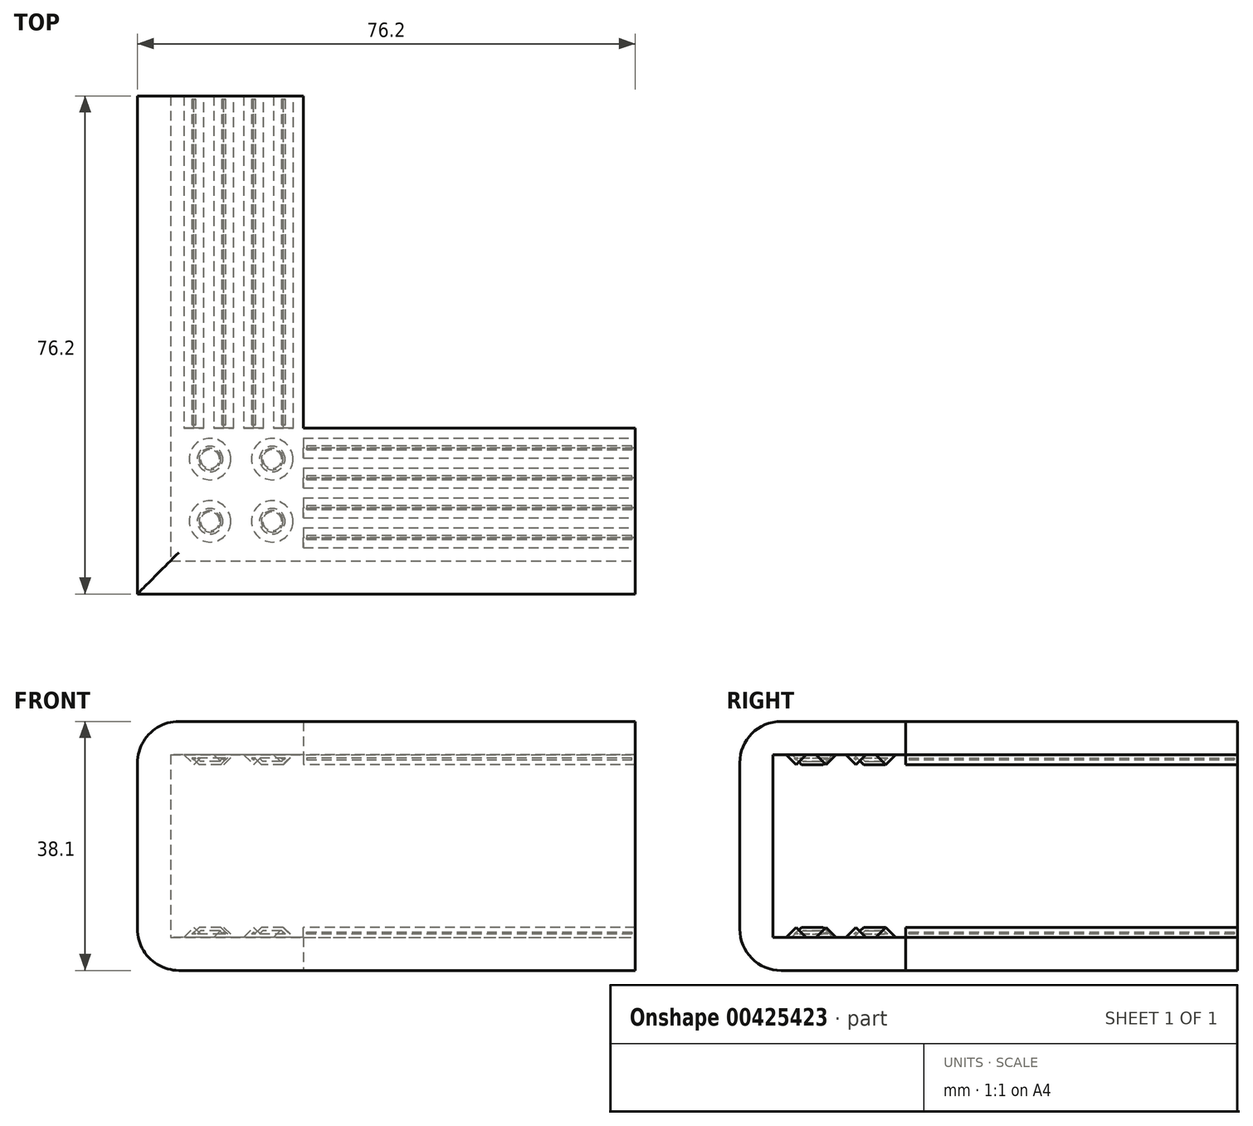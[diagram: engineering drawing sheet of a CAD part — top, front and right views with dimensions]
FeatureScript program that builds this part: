
annotation { "Feature Type Name" : "Feature", "Feature Type Description" : "" }
export const myFeature = defineFeature(function(context is Context, id is Id, definition is map)
    precondition{}
    {
        {
            var Q0;
            Q0=qCreatedBy(makeId("Top.planeOp"),FACE);
            var sketch = newSketch(context, id + "F0", { "sketchPlane" : qUnion([Q0])});
            skLineSegment(sketch, "E0", {"start": v(-49.11, 50.8) * mm, "end": v(-49.11, -25.4) * mm});
            skLineSegment(sketch, "E1", {"start": v(-49.11, -25.4) * mm, "end": v(27.09, -25.4) * mm});
            skLineSegment(sketch, "E2", {"start": v(27.09, -25.4) * mm, "end": v(27.09, 0) * mm});
            skLineSegment(sketch, "E3", {"start": v(27.09, 0) * mm, "end": v(-23.71, 0) * mm});
            skLineSegment(sketch, "E4", {"start": v(-23.71, 0) * mm, "end": v(-23.71, 50.8) * mm});
            skLineSegment(sketch, "E5", {"start": v(-23.71, 50.8) * mm, "end": v(-49.11, 50.8) * mm});
            skSolve(sketch);
        }
        {
            var Q0;
            Q0=makeQuery(id+"F0.imprint","IMPRINT",FACE,{"disambiguationData":[TD([[makeQuery(id+"F0.imprint","IMPRINT",EDGE,{"derivedFrom":sQuery(id+"F0.wireOp",EDGE,"E0")}),1.0]])]});
            extrude(context, id + "F1", {"entities" : qUnion([Q0]), "depth" : 38.1 * mm});
        }
        {
            var Q0;
            Q0=makeQuery(id+"F1.opExtrude","SWEPT_FACE",FACE,{"disambiguationData":[OSD([sQuery(id+"F0.wireOp",EDGE,"E3")])]});
            var Q1;
            Q1=makeQuery(id+"F1.opExtrude","SWEPT_FACE",FACE,{"disambiguationData":[OSD([sQuery(id+"F0.wireOp",EDGE,"E4")])]});
            var Q2;
            Q2=makeQuery(id+"F1.opExtrude","SWEPT_FACE",FACE,{"disambiguationData":[OSD([sQuery(id+"F0.wireOp",EDGE,"E2")])]});
            var Q3;
            Q3=makeQuery(id+"F1.opExtrude","SWEPT_FACE",FACE,{"disambiguationData":[OSD([sQuery(id+"F0.wireOp",EDGE,"E5")])]});
            shell(context, id + "F2", {"entities" : qUnion([Q0, Q1, Q2, Q3]), "thickness" : 5.08 * mm});
        }
        {
            var Q0;
            Q0=makeQuery(id+"F1.opExtrude","CAP_EDGE",EDGE,{"disambiguationData":[OSD([sQuery(id+"F0.wireOp",EDGE,"E1")])],"isStart":false});
            var Q1;
            Q1=makeQuery(id+"F1.opExtrude","CAP_EDGE",EDGE,{"disambiguationData":[OSD([sQuery(id+"F0.wireOp",EDGE,"E0")])],"isStart":false});
            fillet(context, id + "F3", {"entities" : qUnion([Q0, Q1]), "radius" : 6.35 * mm, "tangentPropagation" : true, "allowEdgeOverflow" : false});
        }
        {
            var Q0;
            Q0=makeQuery(id+"F1.opExtrude","CAP_EDGE",EDGE,{"disambiguationData":[OSD([sQuery(id+"F0.wireOp",EDGE,"E0")])],"isStart":true});
            var Q1;
            Q1=makeQuery(id+"F1.opExtrude","CAP_EDGE",EDGE,{"disambiguationData":[OSD([sQuery(id+"F0.wireOp",EDGE,"E1")])],"isStart":true});
            fillet(context, id + "F4", {"entities" : qUnion([Q0, Q1]), "radius" : 6.35 * mm, "tangentPropagation" : true, "allowEdgeOverflow" : false});
        }
        {
            var Q0;
            {var subQ0=sQuery(id+"F0.wireOp",EDGE,"E5");var subQ1=sQuery(id+"F0.wireOp",EDGE,"E4");var subQ2=sQuery(id+"F0.wireOp",EDGE,"E3");var subQ3=sQuery(id+"F0.wireOp",EDGE,"E2");var subQ4=sQuery(id+"F0.wireOp",EDGE,"E1");var subQ5=sQuery(id+"F0.wireOp",EDGE,"E0");Q0=makeQuery(id+"F2.opShell","OFFSET_FACE",FACE,{"disambiguationData":[OSD([subQ5,subQ4,subQ3,subQ2,subQ1,subQ0]),TDD([makeQuery(id+"F1.opExtrude","CAP_FACE",FACE,{"disambiguationData":[OSD([subQ5,subQ4,subQ3,subQ2,subQ1,subQ0])],"isStart":true})])]});}
            var sketch = newSketch(context, id + "F5", { "sketchPlane" : qUnion([Q0])});
            skLineSegment(sketch, "E6", {"start": v(-28.29, 50.8) * mm, "end": v(-25.24, 50.8) * mm});
            skLineSegment(sketch, "E7", {"start": v(-28.29, 50.8) * mm, "end": v(-28.29, 0) * mm});
            skLineSegment(sketch, "E8", {"start": v(-28.29, 0) * mm, "end": v(-25.24, 0) * mm});
            skLineSegment(sketch, "E9", {"start": v(-25.24, 0) * mm, "end": v(-25.24, 50.8) * mm});
            skLineSegment(sketch, "E10.bottom", {"start": v(-23.71, -1.52) * mm, "end": v(27.09, -1.52) * mm});
            skLineSegment(sketch, "E10.top", {"start": v(-23.71, -4.57) * mm, "end": v(27.09, -4.57) * mm});
            skLineSegment(sketch, "E10.left", {"start": v(-23.71, -1.52) * mm, "end": v(-23.71, -4.57) * mm});
            skLineSegment(sketch, "E10.right", {"start": v(27.09, -1.52) * mm, "end": v(27.09, -4.57) * mm});
            skLineSegment(sketch, "E11.0.1.0", {"start": v(-23.71, -6.1) * mm, "end": v(27.09, -6.1) * mm});
            skLineSegment(sketch, "E11.0.1.1", {"start": v(27.09, -6.1) * mm, "end": v(27.09, -9.14) * mm});
            skLineSegment(sketch, "E11.0.1.2", {"start": v(-23.71, -6.1) * mm, "end": v(-23.71, -9.14) * mm});
            skLineSegment(sketch, "E11.0.1.3", {"start": v(-23.71, -9.14) * mm, "end": v(27.09, -9.14) * mm});
            skLineSegment(sketch, "E11.0.2.0", {"start": v(-23.71, -10.67) * mm, "end": v(27.09, -10.67) * mm});
            skLineSegment(sketch, "E11.0.2.1", {"start": v(27.09, -10.67) * mm, "end": v(27.09, -13.72) * mm});
            skLineSegment(sketch, "E11.0.2.2", {"start": v(-23.71, -10.67) * mm, "end": v(-23.71, -13.72) * mm});
            skLineSegment(sketch, "E11.0.2.3", {"start": v(-23.71, -13.72) * mm, "end": v(27.09, -13.72) * mm});
            skLineSegment(sketch, "E11.0.3.0", {"start": v(-23.71, -15.24) * mm, "end": v(27.09, -15.24) * mm});
            skLineSegment(sketch, "E11.0.3.1", {"start": v(27.09, -15.24) * mm, "end": v(27.09, -18.29) * mm});
            skLineSegment(sketch, "E11.0.3.2", {"start": v(-23.71, -15.24) * mm, "end": v(-23.71, -18.29) * mm});
            skLineSegment(sketch, "E11.0.3.3", {"start": v(-23.71, -18.29) * mm, "end": v(27.09, -18.29) * mm});
            skLineSegment(sketch, "E11.direction1", {"start": v(-23.72, -4.57) * mm, "end": v(-23.71, -4.57) * mm, "construction": true});
            skLineSegment(sketch, "E11.direction2", {"start": v(-23.71, -4.57) * mm, "end": v(-23.71, -9.14) * mm, "construction": true});
            skLineSegment(sketch, "E12.1.0.0", {"start": v(-32.86, 50.8) * mm, "end": v(-29.8, 50.8) * mm});
            skLineSegment(sketch, "E12.1.0.1", {"start": v(-32.86, 50.8) * mm, "end": v(-32.86, 0) * mm});
            skLineSegment(sketch, "E12.1.0.2", {"start": v(-32.86, 0) * mm, "end": v(-29.8, 0) * mm});
            skLineSegment(sketch, "E12.1.0.3", {"start": v(-29.8, 0) * mm, "end": v(-29.8, 50.8) * mm});
            skLineSegment(sketch, "E12.2.0.0", {"start": v(-37.43, 50.8) * mm, "end": v(-34.38, 50.8) * mm});
            skLineSegment(sketch, "E12.2.0.1", {"start": v(-37.43, 50.8) * mm, "end": v(-37.43, 0) * mm});
            skLineSegment(sketch, "E12.2.0.2", {"start": v(-37.43, 0) * mm, "end": v(-34.38, 0) * mm});
            skLineSegment(sketch, "E12.2.0.3", {"start": v(-34.38, 0) * mm, "end": v(-34.38, 50.8) * mm});
            skLineSegment(sketch, "E12.3.0.0", {"start": v(-42, 50.8) * mm, "end": v(-38.95, 50.8) * mm});
            skLineSegment(sketch, "E12.3.0.1", {"start": v(-42, 50.8) * mm, "end": v(-42, 0) * mm});
            skLineSegment(sketch, "E12.3.0.2", {"start": v(-42, 0) * mm, "end": v(-38.95, 0) * mm});
            skLineSegment(sketch, "E12.3.0.3", {"start": v(-38.95, 0) * mm, "end": v(-38.95, 50.8) * mm});
            skLineSegment(sketch, "E12.direction1", {"start": v(-28.29, 0) * mm, "end": v(-32.86, 0) * mm, "construction": true});
            skCircle(sketch, "E13", {"center": v(-38, -4.76) * mm, "radius": 3.18 * mm});
            skCircle(sketch, "E14.0.1.0", {"center": v(-38, -14.29) * mm, "radius": 3.18 * mm});
            skCircle(sketch, "E14.1.0.0", {"center": v(-28.48, -4.76) * mm, "radius": 3.18 * mm});
            skCircle(sketch, "E14.1.1.0", {"center": v(-28.48, -14.29) * mm, "radius": 3.18 * mm});
            skLineSegment(sketch, "E14.direction1", {"start": v(-38, -4.76) * mm, "end": v(-28.48, -4.76) * mm, "construction": true});
            skLineSegment(sketch, "E14.direction2", {"start": v(-38, -4.76) * mm, "end": v(-38, -14.29) * mm, "construction": true});
            skLineSegment(sketch, "E15.0.0", {"start": v(-23.71, 50.8) * mm, "end": v(-23.71, 0) * mm});
            skLineSegment(sketch, "E15.0.1", {"start": v(-23.71, 0) * mm, "end": v(27.09, 0) * mm});
            skLineSegment(sketch, "E15.0.2", {"start": v(27.09, 0) * mm, "end": v(27.09, -20.32) * mm});
            skLineSegment(sketch, "E15.0.3", {"start": v(27.09, -20.32) * mm, "end": v(-44.03, -20.32) * mm});
            skLineSegment(sketch, "E15.0.4", {"start": v(-44.03, -20.32) * mm, "end": v(-44.03, 50.8) * mm});
            skLineSegment(sketch, "E15.0.5", {"start": v(-44.03, 50.8) * mm, "end": v(-23.71, 50.8) * mm});
            skLineSegment(sketch, "E16.0", {"start": v(-23.71, 0) * mm, "end": v(-23.71, 50.8) * mm});
            skLineSegment(sketch, "E16.1", {"start": v(27.09, 0) * mm, "end": v(-23.71, 0) * mm});
            skSolve(sketch);
        }
        {
            var Q0;
            {var subQ0=sQuery(id+"F5.wireOp",EDGE,"E10.bottom");Q0=makeQuery(id+"F5.imprint","IMPRINT",FACE,{"disambiguationData":[TD([[makeQuery(id+"F5.imprint","IMPRINT",EDGE,{"derivedFrom":subQ0}),-1.0]])]});}
            var Q1;
            {var subQ0=sQuery(id+"F5.wireOp",EDGE,"E11.0.1.0");Q1=makeQuery(id+"F5.imprint","IMPRINT",FACE,{"disambiguationData":[TD([[makeQuery(id+"F5.imprint","IMPRINT",EDGE,{"derivedFrom":subQ0}),-1.0]])]});}
            var Q2;
            {var subQ0=sQuery(id+"F5.wireOp",EDGE,"E11.0.2.0");Q2=makeQuery(id+"F5.imprint","IMPRINT",FACE,{"disambiguationData":[TD([[makeQuery(id+"F5.imprint","IMPRINT",EDGE,{"derivedFrom":subQ0}),-1.0]])]});}
            var Q3;
            {var subQ0=sQuery(id+"F5.wireOp",EDGE,"E11.0.3.0");Q3=makeQuery(id+"F5.imprint","IMPRINT",FACE,{"disambiguationData":[TD([[makeQuery(id+"F5.imprint","IMPRINT",EDGE,{"derivedFrom":subQ0}),-1.0]])]});}
            var Q4;
            Q4=makeQuery(id+"F5.imprint","IMPRINT",FACE,{"disambiguationData":[TD([[makeQuery(id+"F5.imprint","IMPRINT",EDGE,{"derivedFrom":sQuery(id+"F5.wireOp",EDGE,"E14.0.1.0")}),1.0]])]});
            var Q5;
            {var subQ0=sQuery(id+"F5.wireOp",EDGE,"E12.3.0.1");Q5=makeQuery(id+"F5.imprint","IMPRINT",FACE,{"disambiguationData":[TD([[makeQuery(id+"F5.imprint","IMPRINT",EDGE,{"derivedFrom":subQ0}),1.0]])]});}
            var Q6;
            {var subQ0=sQuery(id+"F5.wireOp",EDGE,"E12.2.0.1");Q6=makeQuery(id+"F5.imprint","IMPRINT",FACE,{"disambiguationData":[TD([[makeQuery(id+"F5.imprint","IMPRINT",EDGE,{"derivedFrom":subQ0}),1.0]])]});}
            var Q7;
            {var subQ0=sQuery(id+"F5.wireOp",EDGE,"E12.1.0.1");Q7=makeQuery(id+"F5.imprint","IMPRINT",FACE,{"disambiguationData":[TD([[makeQuery(id+"F5.imprint","IMPRINT",EDGE,{"derivedFrom":subQ0}),1.0]])]});}
            var Q8;
            {var subQ0=sQuery(id+"F5.wireOp",EDGE,"E7");Q8=makeQuery(id+"F5.imprint","IMPRINT",FACE,{"disambiguationData":[TD([[makeQuery(id+"F5.imprint","IMPRINT",EDGE,{"derivedFrom":subQ0}),1.0]])]});}
            var Q9;
            Q9=makeQuery(id+"F5.imprint","IMPRINT",FACE,{"disambiguationData":[TD([[makeQuery(id+"F5.imprint","IMPRINT",EDGE,{"derivedFrom":sQuery(id+"F5.wireOp",EDGE,"E14.1.0.0")}),1.0]])]});
            var Q10;
            Q10=makeQuery(id+"F5.imprint","IMPRINT",FACE,{"disambiguationData":[TD([[makeQuery(id+"F5.imprint","IMPRINT",EDGE,{"derivedFrom":sQuery(id+"F5.wireOp",EDGE,"E13")}),1.0]])]});
            var Q11;
            Q11=makeQuery(id+"F5.imprint","IMPRINT",FACE,{"disambiguationData":[TD([[makeQuery(id+"F5.imprint","IMPRINT",EDGE,{"derivedFrom":sQuery(id+"F5.wireOp",EDGE,"E14.1.1.0")}),1.0]])]});
            extrude(context, id + "F6", {"entities" : qUnion([Q0, Q1, Q2, Q3, Q4, Q5, Q6, Q7, Q8, Q9, Q10, Q11]), "depth" : 1.52 * mm});
        }
        {
            var Q0;
            Q0=makeQuery(id+"F6.opExtrude","CAP_EDGE",EDGE,{"disambiguationData":[OSD([sQuery(id+"F5.wireOp",EDGE,"E13")])],"isStart":false});
            var Q1;
            Q1=makeQuery(id+"F6.opExtrude","CAP_EDGE",EDGE,{"disambiguationData":[OSD([sQuery(id+"F5.wireOp",EDGE,"E14.1.0.0")])],"isStart":false});
            var Q2;
            Q2=makeQuery(id+"F6.opExtrude","CAP_EDGE",EDGE,{"disambiguationData":[OSD([sQuery(id+"F5.wireOp",EDGE,"E14.0.1.0")])],"isStart":false});
            var Q3;
            Q3=makeQuery(id+"F6.opExtrude","CAP_EDGE",EDGE,{"disambiguationData":[OSD([sQuery(id+"F5.wireOp",EDGE,"E14.1.1.0")])],"isStart":false});
            var Q4;
            Q4=makeQuery(id+"F6.opExtrude","CAP_EDGE",EDGE,{"disambiguationData":[OSD([sQuery(id+"F5.wireOp",EDGE,"E11.0.3.3")])],"isStart":false});
            var Q5;
            Q5=makeQuery(id+"F6.opExtrude","CAP_EDGE",EDGE,{"disambiguationData":[OSD([sQuery(id+"F5.wireOp",EDGE,"E11.0.3.0")])],"isStart":false});
            var Q6;
            Q6=makeQuery(id+"F6.opExtrude","CAP_EDGE",EDGE,{"disambiguationData":[OSD([sQuery(id+"F5.wireOp",EDGE,"E11.0.2.3")])],"isStart":false});
            var Q7;
            Q7=makeQuery(id+"F6.opExtrude","CAP_EDGE",EDGE,{"disambiguationData":[OSD([sQuery(id+"F5.wireOp",EDGE,"E11.0.2.0")])],"isStart":false});
            var Q8;
            Q8=makeQuery(id+"F6.opExtrude","CAP_EDGE",EDGE,{"disambiguationData":[OSD([sQuery(id+"F5.wireOp",EDGE,"E11.0.1.3")])],"isStart":false});
            var Q9;
            Q9=makeQuery(id+"F6.opExtrude","CAP_EDGE",EDGE,{"disambiguationData":[OSD([sQuery(id+"F5.wireOp",EDGE,"E11.0.1.0")])],"isStart":false});
            var Q10;
            Q10=makeQuery(id+"F6.opExtrude","CAP_EDGE",EDGE,{"disambiguationData":[OSD([sQuery(id+"F5.wireOp",EDGE,"E10.top")])],"isStart":false});
            var Q11;
            Q11=makeQuery(id+"F6.opExtrude","CAP_EDGE",EDGE,{"disambiguationData":[OSD([sQuery(id+"F5.wireOp",EDGE,"E10.bottom")])],"isStart":false});
            var Q12;
            Q12=makeQuery(id+"F6.opExtrude","CAP_EDGE",EDGE,{"disambiguationData":[OSD([sQuery(id+"F5.wireOp",EDGE,"E9")])],"isStart":false});
            var Q13;
            Q13=makeQuery(id+"F6.opExtrude","CAP_EDGE",EDGE,{"disambiguationData":[OSD([sQuery(id+"F5.wireOp",EDGE,"E7")])],"isStart":false});
            var Q14;
            Q14=makeQuery(id+"F6.opExtrude","CAP_EDGE",EDGE,{"disambiguationData":[OSD([sQuery(id+"F5.wireOp",EDGE,"E12.1.0.3")])],"isStart":false});
            var Q15;
            Q15=makeQuery(id+"F6.opExtrude","CAP_EDGE",EDGE,{"disambiguationData":[OSD([sQuery(id+"F5.wireOp",EDGE,"E12.1.0.1")])],"isStart":false});
            var Q16;
            Q16=makeQuery(id+"F6.opExtrude","CAP_EDGE",EDGE,{"disambiguationData":[OSD([sQuery(id+"F5.wireOp",EDGE,"E12.2.0.3")])],"isStart":false});
            var Q17;
            Q17=makeQuery(id+"F6.opExtrude","CAP_EDGE",EDGE,{"disambiguationData":[OSD([sQuery(id+"F5.wireOp",EDGE,"E12.2.0.1")])],"isStart":false});
            var Q18;
            Q18=makeQuery(id+"F6.opExtrude","CAP_EDGE",EDGE,{"disambiguationData":[OSD([sQuery(id+"F5.wireOp",EDGE,"E12.3.0.3")])],"isStart":false});
            var Q19;
            Q19=makeQuery(id+"F6.opExtrude","CAP_EDGE",EDGE,{"disambiguationData":[OSD([sQuery(id+"F5.wireOp",EDGE,"E12.3.0.1")])],"isStart":false});
            chamfer(context, id + "F7", {"entities" : qUnion([Q0, Q1, Q2, Q3, Q4, Q5, Q6, Q7, Q8, Q9, Q10, Q11, Q12, Q13, Q14, Q15, Q16, Q17, Q18, Q19]), "width" : 1.52 * mm, "tangentPropagation" : true});
        }
        {
            var Q0;
            Q0=makeQuery(id+"F6.opExtrude","CAP_FACE",FACE,{"disambiguationData":[OSD([sQuery(id+"F5.wireOp",EDGE,"E10.bottom"),sQuery(id+"F5.wireOp",EDGE,"E10.top"),sQuery(id+"F5.wireOp",EDGE,"E10.left"),sQuery(id+"F5.wireOp",EDGE,"E15.0.2")])],"isStart":false});
            var Q1;
            Q1=makeQuery(id+"F6.opExtrude","CAP_FACE",FACE,{"disambiguationData":[OSD([sQuery(id+"F5.wireOp",EDGE,"E11.0.1.0"),sQuery(id+"F5.wireOp",EDGE,"E11.0.1.2"),sQuery(id+"F5.wireOp",EDGE,"E11.0.1.3"),sQuery(id+"F5.wireOp",EDGE,"E15.0.2")])],"isStart":false});
            var Q2;
            Q2=makeQuery(id+"F6.opExtrude","CAP_FACE",FACE,{"disambiguationData":[OSD([sQuery(id+"F5.wireOp",EDGE,"E11.0.2.0"),sQuery(id+"F5.wireOp",EDGE,"E11.0.2.2"),sQuery(id+"F5.wireOp",EDGE,"E11.0.2.3"),sQuery(id+"F5.wireOp",EDGE,"E15.0.2")])],"isStart":false});
            var Q3;
            Q3=makeQuery(id+"F6.opExtrude","CAP_FACE",FACE,{"disambiguationData":[OSD([sQuery(id+"F5.wireOp",EDGE,"E11.0.3.0"),sQuery(id+"F5.wireOp",EDGE,"E11.0.3.2"),sQuery(id+"F5.wireOp",EDGE,"E11.0.3.3"),sQuery(id+"F5.wireOp",EDGE,"E15.0.2")])],"isStart":false});
            var Q4;
            Q4=makeQuery(id+"F6.opExtrude","CAP_FACE",FACE,{"disambiguationData":[OSD([sQuery(id+"F5.wireOp",EDGE,"E14.1.1.0")])],"isStart":false});
            var Q5;
            Q5=makeQuery(id+"F6.opExtrude","CAP_FACE",FACE,{"disambiguationData":[OSD([sQuery(id+"F5.wireOp",EDGE,"E14.0.1.0")])],"isStart":false});
            var Q6;
            Q6=makeQuery(id+"F6.opExtrude","CAP_FACE",FACE,{"disambiguationData":[OSD([sQuery(id+"F5.wireOp",EDGE,"E14.1.0.0")])],"isStart":false});
            var Q7;
            Q7=makeQuery(id+"F6.opExtrude","CAP_FACE",FACE,{"disambiguationData":[OSD([sQuery(id+"F5.wireOp",EDGE,"E13")])],"isStart":false});
            var Q8;
            Q8=makeQuery(id+"F6.opExtrude","CAP_FACE",FACE,{"disambiguationData":[OSD([sQuery(id+"F5.wireOp",EDGE,"E7"),sQuery(id+"F5.wireOp",EDGE,"E8"),sQuery(id+"F5.wireOp",EDGE,"E9"),sQuery(id+"F5.wireOp",EDGE,"E15.0.5")])],"isStart":false});
            var Q9;
            Q9=makeQuery(id+"F6.opExtrude","CAP_FACE",FACE,{"disambiguationData":[OSD([sQuery(id+"F5.wireOp",EDGE,"E12.1.0.1"),sQuery(id+"F5.wireOp",EDGE,"E12.1.0.2"),sQuery(id+"F5.wireOp",EDGE,"E12.1.0.3"),sQuery(id+"F5.wireOp",EDGE,"E15.0.5")])],"isStart":false});
            var Q10;
            Q10=makeQuery(id+"F6.opExtrude","CAP_FACE",FACE,{"disambiguationData":[OSD([sQuery(id+"F5.wireOp",EDGE,"E12.2.0.1"),sQuery(id+"F5.wireOp",EDGE,"E12.2.0.2"),sQuery(id+"F5.wireOp",EDGE,"E12.2.0.3"),sQuery(id+"F5.wireOp",EDGE,"E15.0.5")])],"isStart":false});
            var Q11;
            Q11=makeQuery(id+"F6.opExtrude","CAP_FACE",FACE,{"disambiguationData":[OSD([sQuery(id+"F5.wireOp",EDGE,"E12.3.0.1"),sQuery(id+"F5.wireOp",EDGE,"E12.3.0.2"),sQuery(id+"F5.wireOp",EDGE,"E12.3.0.3"),sQuery(id+"F5.wireOp",EDGE,"E15.0.5")])],"isStart":false});
            var Q12;
            Q12=makeQuery(id+"F6.opExtrude","SWEPT_BODY",BODY,{"disambiguationData":[OSD([sQuery(id+"F5.wireOp",EDGE,"E10.bottom"),sQuery(id+"F5.wireOp",EDGE,"E10.top"),sQuery(id+"F5.wireOp",EDGE,"E10.left"),sQuery(id+"F5.wireOp",EDGE,"E15.0.2")])]});
            var Q13;
            Q13=makeQuery(id+"F6.opExtrude","SWEPT_BODY",BODY,{"disambiguationData":[OSD([sQuery(id+"F5.wireOp",EDGE,"E14.1.1.0")])]});
            var Q14;
            Q14=makeQuery(id+"F6.opExtrude","SWEPT_BODY",BODY,{"disambiguationData":[OSD([sQuery(id+"F5.wireOp",EDGE,"E14.0.1.0")])]});
            var Q15;
            Q15=makeQuery(id+"F6.opExtrude","SWEPT_BODY",BODY,{"disambiguationData":[OSD([sQuery(id+"F5.wireOp",EDGE,"E13")])]});
            var Q16;
            Q16=makeQuery(id+"F6.opExtrude","SWEPT_BODY",BODY,{"disambiguationData":[OSD([sQuery(id+"F5.wireOp",EDGE,"E14.1.0.0")])]});
            var Q17;
            Q17=makeQuery(id+"F6.opExtrude","SWEPT_BODY",BODY,{"disambiguationData":[OSD([sQuery(id+"F5.wireOp",EDGE,"E11.0.1.0"),sQuery(id+"F5.wireOp",EDGE,"E11.0.1.2"),sQuery(id+"F5.wireOp",EDGE,"E11.0.1.3"),sQuery(id+"F5.wireOp",EDGE,"E15.0.2")])]});
            var Q18;
            Q18=makeQuery(id+"F6.opExtrude","SWEPT_BODY",BODY,{"disambiguationData":[OSD([sQuery(id+"F5.wireOp",EDGE,"E11.0.2.0"),sQuery(id+"F5.wireOp",EDGE,"E11.0.2.2"),sQuery(id+"F5.wireOp",EDGE,"E11.0.2.3"),sQuery(id+"F5.wireOp",EDGE,"E15.0.2")])]});
            var Q19;
            Q19=makeQuery(id+"F6.opExtrude","SWEPT_BODY",BODY,{"disambiguationData":[OSD([sQuery(id+"F5.wireOp",EDGE,"E11.0.3.0"),sQuery(id+"F5.wireOp",EDGE,"E11.0.3.2"),sQuery(id+"F5.wireOp",EDGE,"E11.0.3.3"),sQuery(id+"F5.wireOp",EDGE,"E15.0.2")])]});
            var Q20;
            Q20=makeQuery(id+"F6.opExtrude","SWEPT_BODY",BODY,{"disambiguationData":[OSD([sQuery(id+"F5.wireOp",EDGE,"E7"),sQuery(id+"F5.wireOp",EDGE,"E8"),sQuery(id+"F5.wireOp",EDGE,"E9"),sQuery(id+"F5.wireOp",EDGE,"E15.0.5")])]});
            var Q21;
            Q21=makeQuery(id+"F6.opExtrude","SWEPT_BODY",BODY,{"disambiguationData":[OSD([sQuery(id+"F5.wireOp",EDGE,"E12.1.0.1"),sQuery(id+"F5.wireOp",EDGE,"E12.1.0.2"),sQuery(id+"F5.wireOp",EDGE,"E12.1.0.3"),sQuery(id+"F5.wireOp",EDGE,"E15.0.5")])]});
            var Q22;
            Q22=makeQuery(id+"F6.opExtrude","SWEPT_BODY",BODY,{"disambiguationData":[OSD([sQuery(id+"F5.wireOp",EDGE,"E12.2.0.1"),sQuery(id+"F5.wireOp",EDGE,"E12.2.0.2"),sQuery(id+"F5.wireOp",EDGE,"E12.2.0.3"),sQuery(id+"F5.wireOp",EDGE,"E15.0.5")])]});
            var Q23;
            Q23=makeQuery(id+"F6.opExtrude","SWEPT_BODY",BODY,{"disambiguationData":[OSD([sQuery(id+"F5.wireOp",EDGE,"E12.3.0.1"),sQuery(id+"F5.wireOp",EDGE,"E12.3.0.2"),sQuery(id+"F5.wireOp",EDGE,"E12.3.0.3"),sQuery(id+"F5.wireOp",EDGE,"E15.0.5")])]});
            shell(context, id + "F8", {"isHollow" : true, "entities" : qUnion([Q0, Q1, Q2, Q3, Q4, Q5, Q6, Q7, Q8, Q9, Q10, Q11]), "parts" : qUnion([Q12, Q13, Q14, Q15, Q16, Q17, Q18, Q19, Q20, Q21, Q22, Q23]), "thickness" : 0.5 * mm});
        }
        {
            var Q0;
            Q0=makeQuery(id+"F1.opExtrude","SWEPT_EDGE",EDGE,{"disambiguationData":[OSD([sQuery(id+"F0.wireOp",EDGE,"E1"),sQuery(id+"F0.wireOp",EDGE,"E2")])]});
            cPoint(context, id + "F9", {"entities" : qUnion([Q0]), "parameter" : 0.5});
        }
        {
            var Q0;
            Q0=makeQuery(id+"F2.opShell","OFFSET_EDGE",EDGE,{"disambiguationData":[OSD([sQuery(id+"F0.wireOp",EDGE,"E0"),sQuery(id+"F0.wireOp",EDGE,"E5")])]});
            cPoint(context, id + "F10", {"entities" : qUnion([Q0]), "parameter" : 0.5});
        }
        {
            var Q0;
            Q0=makeQuery(id+"F1.opExtrude","SWEPT_EDGE",EDGE,{"disambiguationData":[OSD([sQuery(id+"F0.wireOp",EDGE,"E0"),sQuery(id+"F0.wireOp",EDGE,"E1")])]});
            cPoint(context, id + "F11", {"entities" : qUnion([Q0]), "parameter" : 0.5});
        }
        {
            var Q0;
            Q0=qCreatedBy(id+"F9",VERTEX);
            var Q1;
            Q1=qCreatedBy(id+"F10",VERTEX);
            var Q2;
            Q2=qCreatedBy(id+"F11",VERTEX);
            cPlane(context, id + "F12", {"entities" : qUnion([Q0, Q1, Q2]), "cplaneType" : CPlaneType.THREE_POINT, "offset" : 25.4 * mm, "width" : 152.4 * mm, "height" : 152.4 * mm});
        }
        {
            var Q0;
            Q0=makeQuery(id+"F1.opExtrude","SWEPT_BODY",BODY,{"disambiguationData":[OSD([sQuery(id+"F0.wireOp",EDGE,"E0"),sQuery(id+"F0.wireOp",EDGE,"E1"),sQuery(id+"F0.wireOp",EDGE,"E2"),sQuery(id+"F0.wireOp",EDGE,"E3"),sQuery(id+"F0.wireOp",EDGE,"E4"),sQuery(id+"F0.wireOp",EDGE,"E5")])]});
            var Q1;
            Q1=makeQuery(id+"F6.opExtrude","SWEPT_BODY",BODY,{"disambiguationData":[OSD([sQuery(id+"F5.wireOp",EDGE,"E10.bottom"),sQuery(id+"F5.wireOp",EDGE,"E10.top"),sQuery(id+"F5.wireOp",EDGE,"E10.left"),sQuery(id+"F5.wireOp",EDGE,"E15.0.2")])]});
            var Q2;
            Q2=makeQuery(id+"F6.opExtrude","SWEPT_BODY",BODY,{"disambiguationData":[OSD([sQuery(id+"F5.wireOp",EDGE,"E7"),sQuery(id+"F5.wireOp",EDGE,"E8"),sQuery(id+"F5.wireOp",EDGE,"E9"),sQuery(id+"F5.wireOp",EDGE,"E15.0.5")])]});
            var Q3;
            Q3=makeQuery(id+"F6.opExtrude","SWEPT_BODY",BODY,{"disambiguationData":[OSD([sQuery(id+"F5.wireOp",EDGE,"E14.1.0.0")])]});
            var Q4;
            Q4=makeQuery(id+"F6.opExtrude","SWEPT_BODY",BODY,{"disambiguationData":[OSD([sQuery(id+"F5.wireOp",EDGE,"E14.1.1.0")])]});
            var Q5;
            Q5=makeQuery(id+"F6.opExtrude","SWEPT_BODY",BODY,{"disambiguationData":[OSD([sQuery(id+"F5.wireOp",EDGE,"E11.0.3.0"),sQuery(id+"F5.wireOp",EDGE,"E11.0.3.2"),sQuery(id+"F5.wireOp",EDGE,"E11.0.3.3"),sQuery(id+"F5.wireOp",EDGE,"E15.0.2")])]});
            var Q6;
            Q6=makeQuery(id+"F6.opExtrude","SWEPT_BODY",BODY,{"disambiguationData":[OSD([sQuery(id+"F5.wireOp",EDGE,"E11.0.2.0"),sQuery(id+"F5.wireOp",EDGE,"E11.0.2.2"),sQuery(id+"F5.wireOp",EDGE,"E11.0.2.3"),sQuery(id+"F5.wireOp",EDGE,"E15.0.2")])]});
            var Q7;
            Q7=makeQuery(id+"F6.opExtrude","SWEPT_BODY",BODY,{"disambiguationData":[OSD([sQuery(id+"F5.wireOp",EDGE,"E11.0.1.0"),sQuery(id+"F5.wireOp",EDGE,"E11.0.1.2"),sQuery(id+"F5.wireOp",EDGE,"E11.0.1.3"),sQuery(id+"F5.wireOp",EDGE,"E15.0.2")])]});
            var Q8;
            Q8=makeQuery(id+"F6.opExtrude","SWEPT_BODY",BODY,{"disambiguationData":[OSD([sQuery(id+"F5.wireOp",EDGE,"E14.0.1.0")])]});
            var Q9;
            Q9=makeQuery(id+"F6.opExtrude","SWEPT_BODY",BODY,{"disambiguationData":[OSD([sQuery(id+"F5.wireOp",EDGE,"E13")])]});
            var Q10;
            Q10=makeQuery(id+"F6.opExtrude","SWEPT_BODY",BODY,{"disambiguationData":[OSD([sQuery(id+"F5.wireOp",EDGE,"E12.1.0.1"),sQuery(id+"F5.wireOp",EDGE,"E12.1.0.2"),sQuery(id+"F5.wireOp",EDGE,"E12.1.0.3"),sQuery(id+"F5.wireOp",EDGE,"E15.0.5")])]});
            var Q11;
            Q11=makeQuery(id+"F6.opExtrude","SWEPT_BODY",BODY,{"disambiguationData":[OSD([sQuery(id+"F5.wireOp",EDGE,"E12.2.0.1"),sQuery(id+"F5.wireOp",EDGE,"E12.2.0.2"),sQuery(id+"F5.wireOp",EDGE,"E12.2.0.3"),sQuery(id+"F5.wireOp",EDGE,"E15.0.5")])]});
            var Q12;
            Q12=makeQuery(id+"F6.opExtrude","SWEPT_BODY",BODY,{"disambiguationData":[OSD([sQuery(id+"F5.wireOp",EDGE,"E12.3.0.1"),sQuery(id+"F5.wireOp",EDGE,"E12.3.0.2"),sQuery(id+"F5.wireOp",EDGE,"E12.3.0.3"),sQuery(id+"F5.wireOp",EDGE,"E15.0.5")])]});
            var Q13;
            Q13=qCreatedBy(id+"F12.planeOp",FACE);
            mirror(context, id + "F13", {"entities" : qUnion([Q0, Q1, Q2, Q3, Q4, Q5, Q6, Q7, Q8, Q9, Q10, Q11, Q12]), "mirrorPlane" : qUnion([Q13])});
        }
    });
